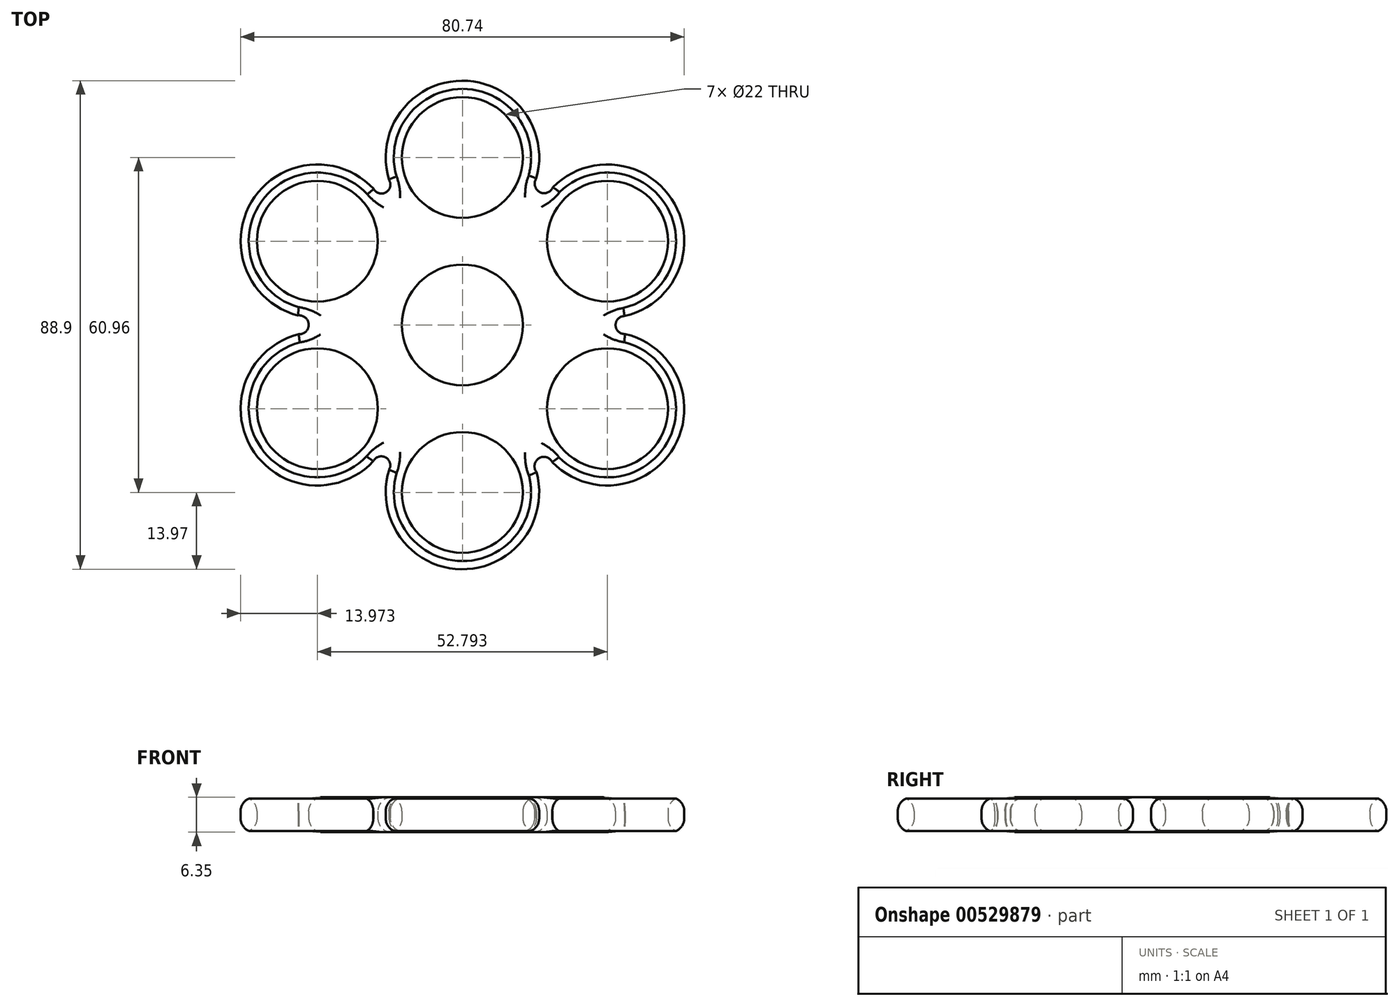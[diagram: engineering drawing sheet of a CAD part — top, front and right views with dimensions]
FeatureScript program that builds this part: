
annotation { "Feature Type Name" : "Feature", "Feature Type Description" : "" }
export const myFeature = defineFeature(function(context is Context, id is Id, definition is map)
    precondition{}
    {
        {
            var Q0;
            Q0=qCreatedBy(makeId("Top.planeOp"),FACE);
            var sketch = newSketch(context, id + "F0", { "sketchPlane" : qUnion([Q0])});
            skCircle(sketch, "E0", {"center": v(0, 0) * mm, "radius": 44.45 * mm});
            skCircle(sketch, "E1", {"center": v(0, 0) * mm, "radius": 11 * mm});
            skCircle(sketch, "E2", {"center": v(0, 30.48) * mm, "radius": 11 * mm});
            skPoint(sketch, "E3.center", {"position": v(2.54, -4.43) * mm});
            skCircle(sketch, "E4.1.0", {"center": v(-26.4, -15.24) * mm, "radius": 11 * mm});
            skCircle(sketch, "E4.2.0", {"center": v(26.4, -15.24) * mm, "radius": 11 * mm});
            skLineSegment(sketch, "E5", {"start": v(0, 0) * mm, "end": v(0, -30.48) * mm});
            skCircle(sketch, "E6", {"center": v(0, -30.48) * mm, "radius": 11 * mm});
            skCircle(sketch, "E7.1.0", {"center": v(26.4, 15.24) * mm, "radius": 11 * mm});
            skCircle(sketch, "E7.2.0", {"center": v(-26.4, 15.24) * mm, "radius": 11 * mm});
            skCircle(sketch, "E8.2.0", {"center": v(26.4, 15.24) * mm, "radius": 13.97 * mm});
            skCircle(sketch, "E9.1.0", {"center": v(26.4, -15.24) * mm, "radius": 13.97 * mm});
            skCircle(sketch, "E10", {"center": v(0, 0) * mm, "radius": 13.97 * mm});
            skCircle(sketch, "E11.1.0", {"center": v(-26.4, 15.24) * mm, "radius": 13.97 * mm});
            skCircle(sketch, "E11.2.0", {"center": v(0, -30.48) * mm, "radius": 13.97 * mm});
            skCircle(sketch, "E12.1.0", {"center": v(0, 30.48) * mm, "radius": 13.97 * mm});
            skCircle(sketch, "E12.2.0", {"center": v(-26.4, -15.24) * mm, "radius": 13.97 * mm});
            skArc(sketch, "E13", {"start": v(-13.34, -26.34) * mm, "mid": v(-14, -24.1) * mm, "end": v(-16.22, -24.8) * mm});
            skArc(sketch, "E14.1.0", {"start": v(29.48, 1.61) * mm, "mid": v(27.86, -0.07) * mm, "end": v(29.6, -1.64) * mm});
            skArc(sketch, "E14.2.0", {"start": v(-16.14, 24.72) * mm, "mid": v(-13.87, 24.16) * mm, "end": v(-13.37, 26.45) * mm});
            skArc(sketch, "E15", {"start": v(-29.79, -1.69) * mm, "mid": v(-27.97, 0.1) * mm, "end": v(-29.92, 1.72) * mm});
            skArc(sketch, "E16.1.0", {"start": v(16.35, -24.95) * mm, "mid": v(13.9, -24.27) * mm, "end": v(13.47, -26.77) * mm});
            skArc(sketch, "E16.2.0", {"start": v(13.43, 26.64) * mm, "mid": v(14.06, 24.18) * mm, "end": v(16.45, 25.05) * mm});
            skSolve(sketch);
        }
        {
            var Q0;
            Q0=makeQuery(id+"F0.imprint","IMPRINT",FACE,{"disambiguationData":[TD([[makeQuery(id+"F0.imprint","IMPRINT",EDGE,{"derivedFrom":sQuery(id+"F0.wireOp",EDGE,"E10")}),-1.0]])]});
            var Q1;
            Q1=makeQuery(id+"F0.imprint","IMPRINT",FACE,{"disambiguationData":[TD([[makeQuery(id+"F0.imprint","IMPRINT",EDGE,{"derivedFrom":sQuery(id+"F0.wireOp",EDGE,"E1")}),-1.0]])]});
            var Q2;
            Q2=makeQuery(id+"F0.imprint","IMPRINT",FACE,{"disambiguationData":[TD([[makeQuery(id+"F0.imprint","IMPRINT",EDGE,{"derivedFrom":sQuery(id+"F0.wireOp",EDGE,"E7.1.0")}),-1.0]])]});
            var Q3;
            Q3=makeQuery(id+"F0.imprint","IMPRINT",FACE,{"disambiguationData":[TD([[makeQuery(id+"F0.imprint","IMPRINT",EDGE,{"derivedFrom":sQuery(id+"F0.wireOp",EDGE,"E2")}),-1.0]])]});
            var Q4;
            Q4=makeQuery(id+"F0.imprint","IMPRINT",FACE,{"disambiguationData":[TD([[makeQuery(id+"F0.imprint","IMPRINT",EDGE,{"derivedFrom":sQuery(id+"F0.wireOp",EDGE,"E7.2.0")}),-1.0]])]});
            var Q5;
            Q5=makeQuery(id+"F0.imprint","IMPRINT",FACE,{"disambiguationData":[TD([[makeQuery(id+"F0.imprint","IMPRINT",EDGE,{"derivedFrom":sQuery(id+"F0.wireOp",EDGE,"E4.1.0")}),-1.0]])]});
            var Q6;
            Q6=makeQuery(id+"F0.imprint","IMPRINT",FACE,{"disambiguationData":[TD([[makeQuery(id+"F0.imprint","IMPRINT",EDGE,{"derivedFrom":sQuery(id+"F0.wireOp",EDGE,"E6")}),-1.0]])]});
            var Q7;
            Q7=makeQuery(id+"F0.imprint","IMPRINT",FACE,{"disambiguationData":[TD([[makeQuery(id+"F0.imprint","IMPRINT",EDGE,{"derivedFrom":sQuery(id+"F0.wireOp",EDGE,"E4.2.0")}),-1.0]])]});
            extrude(context, id + "F1", {"entities" : qUnion([Q0, Q1, Q2, Q3, Q4, Q5, Q6, Q7]), "depth" : 6.35 * mm, "offsetDistance" : 25.4 * mm});
        }
        {
            var Q0;
            Q0=makeQuery(id+"F1.opExtrude","CAP_EDGE",EDGE,{"disambiguationData":[OSD([sQuery(id+"F0.wireOp",EDGE,"E14.2.0")])],"isStart":false});
            var Q1;
            Q1=makeQuery(id+"F1.opExtrude","CAP_EDGE",EDGE,{"disambiguationData":[OSD([sQuery(id+"F0.wireOp",EDGE,"E16.2.0")])],"isStart":false});
            var Q2;
            Q2=makeQuery(id+"F1.opExtrude","CAP_EDGE",EDGE,{"disambiguationData":[OSD([sQuery(id+"F0.wireOp",EDGE,"E14.1.0")])],"isStart":false});
            var Q3;
            Q3=makeQuery(id+"F1.opExtrude","CAP_EDGE",EDGE,{"disambiguationData":[OSD([sQuery(id+"F0.wireOp",EDGE,"E16.1.0")])],"isStart":false});
            var Q4;
            Q4=makeQuery(id+"F1.opExtrude","CAP_EDGE",EDGE,{"disambiguationData":[OSD([sQuery(id+"F0.wireOp",EDGE,"E13")])],"isStart":false});
            var Q5;
            Q5=makeQuery(id+"F1.opExtrude","CAP_EDGE",EDGE,{"disambiguationData":[OSD([sQuery(id+"F0.wireOp",EDGE,"E15")])],"isStart":false});
            var Q6;
            Q6=makeQuery(id+"F1.opExtrude","CAP_EDGE",EDGE,{"disambiguationData":[OSD([sQuery(id+"F0.wireOp",EDGE,"E12.2.0")])],"isStart":false});
            var Q7;
            Q7=makeQuery(id+"F1.opExtrude","CAP_EDGE",EDGE,{"disambiguationData":[OSD([sQuery(id+"F0.wireOp",EDGE,"E11.1.0")])],"isStart":false});
            var Q8;
            Q8=makeQuery(id+"F1.opExtrude","CAP_EDGE",EDGE,{"disambiguationData":[OSD([sQuery(id+"F0.wireOp",EDGE,"E12.1.0")])],"isStart":false});
            var Q9;
            Q9=makeQuery(id+"F1.opExtrude","CAP_EDGE",EDGE,{"disambiguationData":[OSD([sQuery(id+"F0.wireOp",EDGE,"E8.2.0")])],"isStart":false});
            var Q10;
            Q10=makeQuery(id+"F1.opExtrude","CAP_EDGE",EDGE,{"disambiguationData":[OSD([sQuery(id+"F0.wireOp",EDGE,"E9.1.0")])],"isStart":false});
            var Q11;
            Q11=makeQuery(id+"F1.opExtrude","CAP_EDGE",EDGE,{"disambiguationData":[OSD([sQuery(id+"F0.wireOp",EDGE,"E11.2.0")])],"isStart":false});
            var Q12;
            Q12=makeQuery(id+"F1.opExtrude","CAP_FACE",FACE,{"disambiguationData":[OSD([sQuery(id+"F0.wireOp",EDGE,"E1"),sQuery(id+"F0.wireOp",EDGE,"E2"),sQuery(id+"F0.wireOp",EDGE,"E4.1.0"),sQuery(id+"F0.wireOp",EDGE,"E4.2.0"),sQuery(id+"F0.wireOp",EDGE,"E6"),sQuery(id+"F0.wireOp",EDGE,"E7.1.0"),sQuery(id+"F0.wireOp",EDGE,"E7.2.0"),sQuery(id+"F0.wireOp",EDGE,"E8.2.0"),sQuery(id+"F0.wireOp",EDGE,"E9.1.0"),sQuery(id+"F0.wireOp",EDGE,"E11.1.0"),sQuery(id+"F0.wireOp",EDGE,"E11.2.0"),sQuery(id+"F0.wireOp",EDGE,"E12.1.0"),sQuery(id+"F0.wireOp",EDGE,"E12.2.0"),sQuery(id+"F0.wireOp",EDGE,"E13"),sQuery(id+"F0.wireOp",EDGE,"E14.1.0"),sQuery(id+"F0.wireOp",EDGE,"E14.2.0"),sQuery(id+"F0.wireOp",EDGE,"E15"),sQuery(id+"F0.wireOp",EDGE,"E16.1.0"),sQuery(id+"F0.wireOp",EDGE,"E16.2.0")])],"isStart":false});
            var Q13;
            Q13=makeQuery(id+"F1.opExtrude","CAP_EDGE",EDGE,{"disambiguationData":[OSD([sQuery(id+"F0.wireOp",EDGE,"E14.1.0")])],"isStart":true});
            var Q14;
            Q14=makeQuery(id+"F1.opExtrude","CAP_EDGE",EDGE,{"disambiguationData":[OSD([sQuery(id+"F0.wireOp",EDGE,"E16.1.0")])],"isStart":true});
            var Q15;
            Q15=makeQuery(id+"F1.opExtrude","CAP_EDGE",EDGE,{"disambiguationData":[OSD([sQuery(id+"F0.wireOp",EDGE,"E13")])],"isStart":true});
            var Q16;
            Q16=makeQuery(id+"F1.opExtrude","CAP_EDGE",EDGE,{"disambiguationData":[OSD([sQuery(id+"F0.wireOp",EDGE,"E15")])],"isStart":true});
            var Q17;
            Q17=makeQuery(id+"F1.opExtrude","CAP_EDGE",EDGE,{"disambiguationData":[OSD([sQuery(id+"F0.wireOp",EDGE,"E14.2.0")])],"isStart":true});
            var Q18;
            Q18=makeQuery(id+"F1.opExtrude","CAP_EDGE",EDGE,{"disambiguationData":[OSD([sQuery(id+"F0.wireOp",EDGE,"E16.2.0")])],"isStart":true});
            var Q19;
            Q19=makeQuery(id+"F1.opExtrude","CAP_EDGE",EDGE,{"disambiguationData":[OSD([sQuery(id+"F0.wireOp",EDGE,"E12.1.0")])],"isStart":true});
            var Q20;
            Q20=makeQuery(id+"F1.opExtrude","CAP_EDGE",EDGE,{"disambiguationData":[OSD([sQuery(id+"F0.wireOp",EDGE,"E8.2.0")])],"isStart":true});
            var Q21;
            Q21=makeQuery(id+"F1.opExtrude","CAP_FACE",FACE,{"disambiguationData":[OSD([sQuery(id+"F0.wireOp",EDGE,"E1"),sQuery(id+"F0.wireOp",EDGE,"E2"),sQuery(id+"F0.wireOp",EDGE,"E4.1.0"),sQuery(id+"F0.wireOp",EDGE,"E4.2.0"),sQuery(id+"F0.wireOp",EDGE,"E6"),sQuery(id+"F0.wireOp",EDGE,"E7.1.0"),sQuery(id+"F0.wireOp",EDGE,"E7.2.0"),sQuery(id+"F0.wireOp",EDGE,"E8.2.0"),sQuery(id+"F0.wireOp",EDGE,"E9.1.0"),sQuery(id+"F0.wireOp",EDGE,"E11.1.0"),sQuery(id+"F0.wireOp",EDGE,"E11.2.0"),sQuery(id+"F0.wireOp",EDGE,"E12.1.0"),sQuery(id+"F0.wireOp",EDGE,"E12.2.0"),sQuery(id+"F0.wireOp",EDGE,"E13"),sQuery(id+"F0.wireOp",EDGE,"E14.1.0"),sQuery(id+"F0.wireOp",EDGE,"E14.2.0"),sQuery(id+"F0.wireOp",EDGE,"E15"),sQuery(id+"F0.wireOp",EDGE,"E16.1.0"),sQuery(id+"F0.wireOp",EDGE,"E16.2.0")])],"isStart":true});
            var Q22;
            Q22=makeQuery(id+"F1.opExtrude","CAP_EDGE",EDGE,{"disambiguationData":[OSD([sQuery(id+"F0.wireOp",EDGE,"E7.2.0")])],"isStart":false});
            var Q23;
            Q23=makeQuery(id+"F1.opExtrude","CAP_EDGE",EDGE,{"disambiguationData":[OSD([sQuery(id+"F0.wireOp",EDGE,"E2")])],"isStart":false});
            var Q24;
            Q24=makeQuery(id+"F1.opExtrude","CAP_EDGE",EDGE,{"disambiguationData":[OSD([sQuery(id+"F0.wireOp",EDGE,"E7.1.0")])],"isStart":false});
            var Q25;
            Q25=makeQuery(id+"F1.opExtrude","CAP_EDGE",EDGE,{"disambiguationData":[OSD([sQuery(id+"F0.wireOp",EDGE,"E4.2.0")])],"isStart":false});
            var Q26;
            Q26=makeQuery(id+"F1.opExtrude","CAP_EDGE",EDGE,{"disambiguationData":[OSD([sQuery(id+"F0.wireOp",EDGE,"E6")])],"isStart":false});
            var Q27;
            Q27=makeQuery(id+"F1.opExtrude","CAP_EDGE",EDGE,{"disambiguationData":[OSD([sQuery(id+"F0.wireOp",EDGE,"E4.1.0")])],"isStart":false});
            fillet(context, id + "F2", {"entities" : qUnion([Q0, Q1, Q2, Q3, Q4, Q5, Q6, Q7, Q8, Q9, Q10, Q11, Q12, Q13, Q14, Q15, Q16, Q17, Q18, Q19, Q20, Q21, Q22, Q23, Q24, Q25, Q26, Q27]), "radius" : 2.54 * mm, "tangentPropagation" : true, "allowEdgeOverflow" : false});
        }
    });
